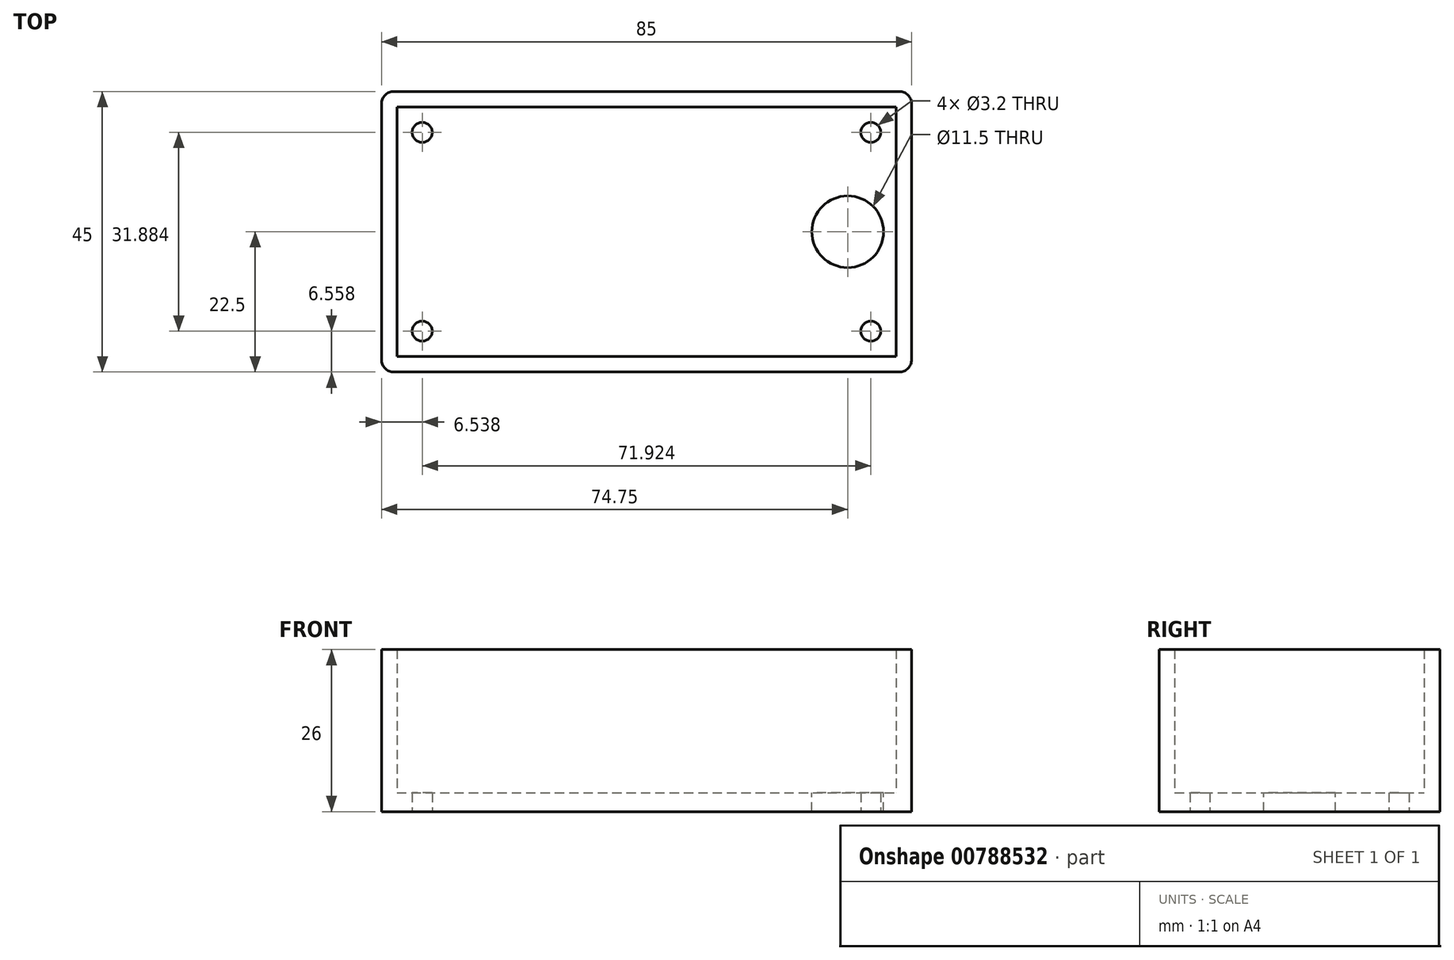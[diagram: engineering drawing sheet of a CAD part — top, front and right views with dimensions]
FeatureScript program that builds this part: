
annotation { "Feature Type Name" : "Feature", "Feature Type Description" : "" }
export const myFeature = defineFeature(function(context is Context, id is Id, definition is map)
    precondition{}
    {
        {
            var Q0;
            Q0=qCreatedBy(makeId("Top.planeOp"),FACE);
            var sketch = newSketch(context, id + "F0", { "sketchPlane" : qUnion([Q0])});
            skLineSegment(sketch, "E0.bottom", {"start": v(40, 20) * mm, "end": v(-40, 20) * mm});
            skLineSegment(sketch, "E0.top", {"start": v(40, -20) * mm, "end": v(-40, -20) * mm});
            skLineSegment(sketch, "E0.left", {"start": v(40, 20) * mm, "end": v(40, -20) * mm});
            skLineSegment(sketch, "E0.right", {"start": v(-40, 20) * mm, "end": v(-40, -20) * mm});
            skPoint(sketch, "E0.middle", {"position": v(0, 0) * mm});
            skLineSegment(sketch, "E1.bottom", {"start": v(42.5, 22.5) * mm, "end": v(-42.5, 22.5) * mm});
            skLineSegment(sketch, "E1.top", {"start": v(42.5, -22.5) * mm, "end": v(-42.5, -22.5) * mm});
            skLineSegment(sketch, "E1.left", {"start": v(42.5, 22.5) * mm, "end": v(42.5, -22.5) * mm});
            skLineSegment(sketch, "E1.right", {"start": v(-42.5, 22.5) * mm, "end": v(-42.5, -22.5) * mm});
            skSolve(sketch);
        }
        {
            var Q0;
            Q0=makeQuery(id+"F0.imprint","IMPRINT",FACE,{"disambiguationData":[TD([[makeQuery(id+"F0.imprint","IMPRINT",EDGE,{"derivedFrom":sQuery(id+"F0.wireOp",EDGE,"E0.bottom")}),-1.0]])]});
            var Q1;
            Q1=makeQuery(id+"F0.imprint","IMPRINT",FACE,{"disambiguationData":[TD([[makeQuery(id+"F0.imprint","IMPRINT",EDGE,{"derivedFrom":sQuery(id+"F0.wireOp",EDGE,"E0.bottom")}),1.0]])]});
            extrude(context, id + "F1", {"entities" : qUnion([Q0, Q1]), "depth" : 3 * mm, "offsetDistance" : 25 * mm});
        }
        {
            var Q0;
            Q0=makeQuery(id+"F0.imprint","IMPRINT",FACE,{"disambiguationData":[TD([[makeQuery(id+"F0.imprint","IMPRINT",EDGE,{"derivedFrom":sQuery(id+"F0.wireOp",EDGE,"E0.bottom")}),-1.0]])]});
            extrude(context, id + "F2", {"entities" : qUnion([Q0]), "operationType" : NewBodyOperationType.ADD, "depth" : 26 * mm, "offsetDistance" : 25 * mm});
        }
        {
            var Q0;
            {var subQ0=sQuery(id+"F0.wireOp",EDGE,"E1.right");var subQ1=sQuery(id+"F0.wireOp",EDGE,"E1.top");Q0=makeQuery(id+"F2.boolean.opBoolean","MERGE",EDGE,{"derivedFrom":[makeQuery(id+"F1.opExtrude","SWEPT_EDGE",EDGE,{"disambiguationData":[OSD([subQ1,subQ0])]}),makeQuery(id+"F2.opExtrude","SWEPT_EDGE",EDGE,{"disambiguationData":[OSD([subQ1,subQ0])]})]});}
            var Q1;
            {var subQ0=sQuery(id+"F0.wireOp",EDGE,"E1.left");var subQ1=sQuery(id+"F0.wireOp",EDGE,"E1.top");Q1=makeQuery(id+"F2.boolean.opBoolean","MERGE",EDGE,{"derivedFrom":[makeQuery(id+"F1.opExtrude","SWEPT_EDGE",EDGE,{"disambiguationData":[OSD([subQ1,subQ0])]}),makeQuery(id+"F2.opExtrude","SWEPT_EDGE",EDGE,{"disambiguationData":[OSD([subQ1,subQ0])]})]});}
            var Q2;
            {var subQ0=sQuery(id+"F0.wireOp",EDGE,"E1.right");var subQ1=sQuery(id+"F0.wireOp",EDGE,"E1.bottom");Q2=makeQuery(id+"F2.boolean.opBoolean","MERGE",EDGE,{"derivedFrom":[makeQuery(id+"F1.opExtrude","SWEPT_EDGE",EDGE,{"disambiguationData":[OSD([subQ1,subQ0])]}),makeQuery(id+"F2.opExtrude","SWEPT_EDGE",EDGE,{"disambiguationData":[OSD([subQ1,subQ0])]})]});}
            var Q3;
            {var subQ0=sQuery(id+"F0.wireOp",EDGE,"E1.left");var subQ1=sQuery(id+"F0.wireOp",EDGE,"E1.bottom");Q3=makeQuery(id+"F2.boolean.opBoolean","MERGE",EDGE,{"derivedFrom":[makeQuery(id+"F1.opExtrude","SWEPT_EDGE",EDGE,{"disambiguationData":[OSD([subQ1,subQ0])]}),makeQuery(id+"F2.opExtrude","SWEPT_EDGE",EDGE,{"disambiguationData":[OSD([subQ1,subQ0])]})]});}
            fillet(context, id + "F3", {"entities" : qUnion([Q0, Q1, Q2, Q3]), "radius" : 2 * mm, "tangentPropagation" : true, "allowEdgeOverflow" : false});
        }
        {
            var Q0;
            Q0=makeQuery(id+"F1.opExtrude","CAP_FACE",FACE,{"disambiguationData":[OSD([sQuery(id+"F0.wireOp",EDGE,"E1.bottom"),sQuery(id+"F0.wireOp",EDGE,"E1.top"),sQuery(id+"F0.wireOp",EDGE,"E1.left"),sQuery(id+"F0.wireOp",EDGE,"E1.right")])],"isStart":false});
            var sketch = newSketch(context, id + "F4", { "sketchPlane" : qUnion([Q0])});
            skCircle(sketch, "E2", {"center": v(32.25, 0) * mm, "radius": 5.75 * mm});
            skSolve(sketch);
        }
        {
            var Q0;
            Q0=makeQuery(id+"F4.imprint","IMPRINT",FACE,{"disambiguationData":[TD([[makeQuery(id+"F4.imprint","IMPRINT",EDGE,{"derivedFrom":sQuery(id+"F4.wireOp",EDGE,"E2")}),1.0]])]});
            extrude(context, id + "F5", {"entities" : qUnion([Q0]), "operationType" : NewBodyOperationType.REMOVE, "endBound" : BoundingType.UP_TO_NEXT, "oppositeDirection" : true, "depth" : 25 * mm, "offsetDistance" : 25 * mm});
        }
        {
            var Q0;
            Q0=makeQuery(id+"F1.opExtrude","CAP_FACE",FACE,{"disambiguationData":[OSD([sQuery(id+"F0.wireOp",EDGE,"E1.bottom"),sQuery(id+"F0.wireOp",EDGE,"E1.top"),sQuery(id+"F0.wireOp",EDGE,"E1.left"),sQuery(id+"F0.wireOp",EDGE,"E1.right")])],"isStart":true});
            var sketch = newSketch(context, id + "F6", { "sketchPlane" : qUnion([Q0])});
            skCircle(sketch, "E3", {"center": v(-35.96, -15.94) * mm, "radius": 1.6 * mm});
            skCircle(sketch, "E4.MirrorC", {"center": v(-35.96, 15.94) * mm, "radius": 1.6 * mm});
            skCircle(sketch, "E5.MirrorC", {"center": v(35.96, 15.94) * mm, "radius": 1.6 * mm});
            skCircle(sketch, "E6.MirrorC", {"center": v(35.96, -15.94) * mm, "radius": 1.6 * mm});
            skSolve(sketch);
        }
        {
            var Q0;
            Q0 = qSketchRegion(id + "F6", true);
            extrude(context, id + "F7", {"entities" : qUnion([Q0]), "operationType" : NewBodyOperationType.REMOVE, "oppositeDirection" : true, "depth" : 25 * mm, "offsetDistance" : 25 * mm});
        }
    });
